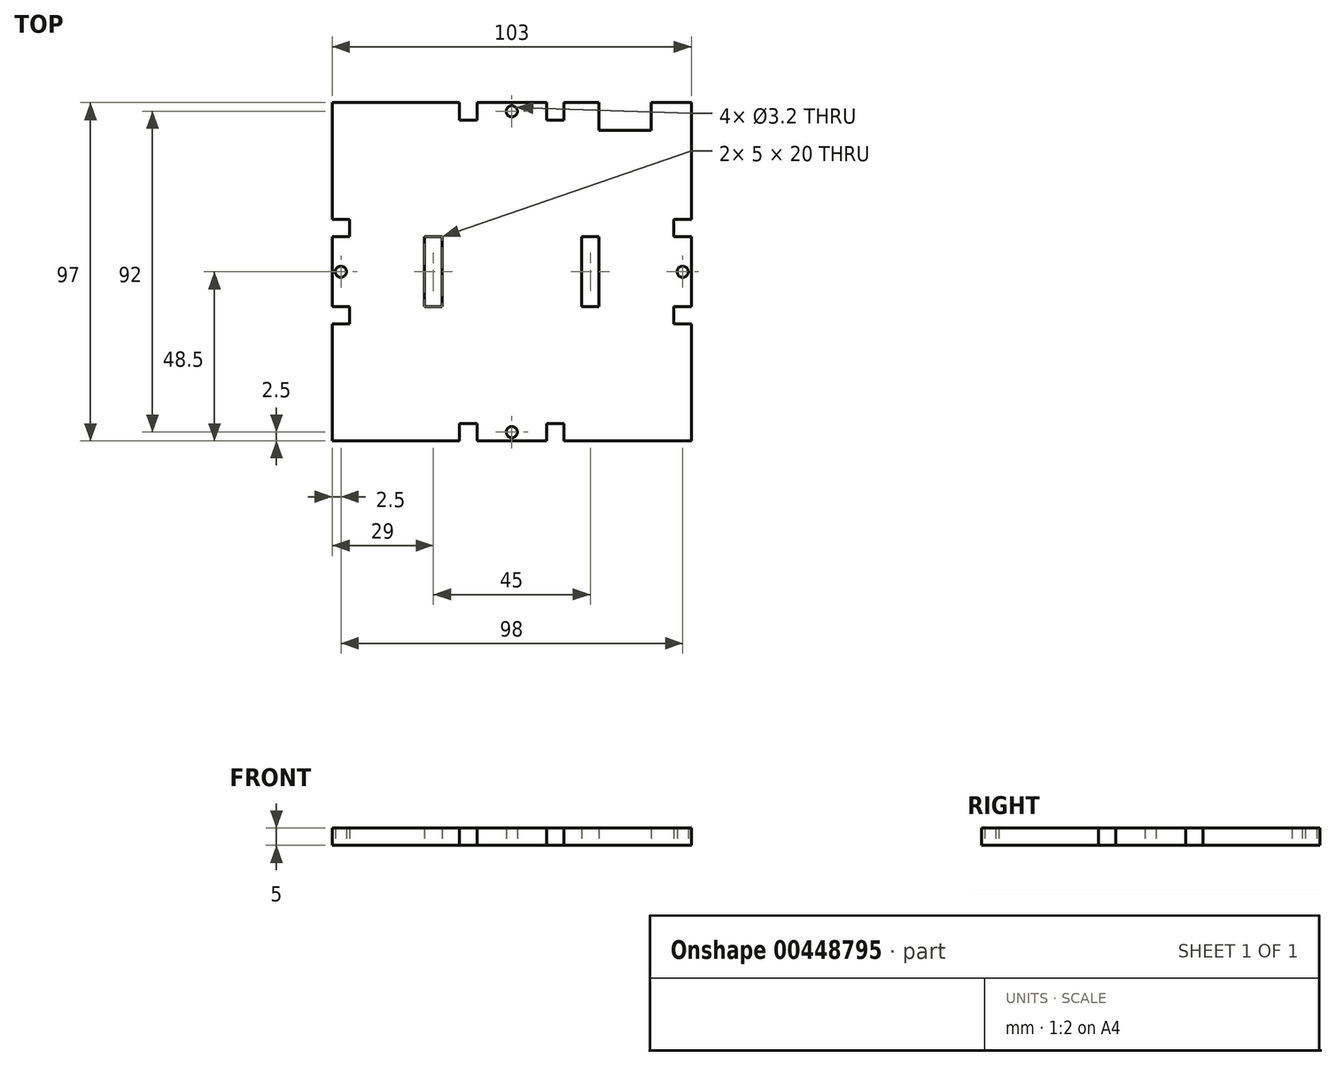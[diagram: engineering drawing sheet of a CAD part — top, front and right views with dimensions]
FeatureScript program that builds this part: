
annotation { "Feature Type Name" : "Feature", "Feature Type Description" : "" }
export const myFeature = defineFeature(function(context is Context, id is Id, definition is map)
    precondition{}
    {
        {
            assignVariable(context, id + "F0", {"name" : "thickness", "anyValue" : 5 * mm});
        }
        {
            var Q0;
            Q0=qCreatedBy(makeId("Top.planeOp"),FACE);
            var sketch = newSketch(context, id + "F1", { "sketchPlane" : qUnion([Q0])});
            skLineSegment(sketch, "E0.MirrorCS", {"start": v(41.5, 92) * mm, "end": v(41.5, 97) * mm});
            skPoint(sketch, "E1.MirrorP", {"position": v(41.5, 94.5) * mm});
            skLineSegment(sketch, "E2.MirrorCS", {"start": v(61.5, 92) * mm, "end": v(66.5, 92) * mm});
            skLineSegment(sketch, "E3.MirrorCS", {"start": v(36.5, 97) * mm, "end": v(36.5, 92) * mm});
            skLineSegment(sketch, "E4.MirrorCS", {"start": v(36.5, 92) * mm, "end": v(41.5, 92) * mm});
            skCircle(sketch, "E5.MirrorC", {"center": v(51.5, 94.5) * mm, "radius": 1.6 * mm});
            skLineSegment(sketch, "E6.MirrorCS", {"start": v(61.5, 97) * mm, "end": v(61.5, 92) * mm});
            skLineSegment(sketch, "E7.MirrorCS", {"start": v(66.5, 92) * mm, "end": v(66.5, 97) * mm});
            skLineSegment(sketch, "E8.MirrorCS", {"start": v(41.5, 97) * mm, "end": v(61.5, 97) * mm});
            skLineSegment(sketch, "E9.bottom", {"start": v(0, 0) * mm, "end": v(36.5, 0) * mm});
            skLineSegment(sketch, "E9.top", {"start": v(0, 97) * mm, "end": v(36.5, 97) * mm});
            skLineSegment(sketch, "E9.left", {"start": v(0, 0) * mm, "end": v(0, 33.5) * mm});
            skLineSegment(sketch, "E9.right", {"start": v(103, 0) * mm, "end": v(103, 33.5) * mm});
            skLineSegment(sketch, "E10", {"start": v(51.5, 0) * mm, "end": v(51.5, 97) * mm, "construction": true});
            skLineSegment(sketch, "E11", {"start": v(0, 48.5) * mm, "end": v(103, 48.5) * mm, "construction": true});
            skLineSegment(sketch, "E12.MirrorCS", {"start": v(41.5, 5) * mm, "end": v(41.5, 0) * mm});
            skLineSegment(sketch, "E13.MirrorCS", {"start": v(41.5, 0) * mm, "end": v(61.5, 0) * mm});
            skLineSegment(sketch, "E14.MirrorCS", {"start": v(61.5, 0) * mm, "end": v(61.5, 5) * mm});
            skLineSegment(sketch, "E15.MirrorCS", {"start": v(66.5, 5) * mm, "end": v(66.5, 0) * mm});
            skPoint(sketch, "E16.MirrorP", {"position": v(41.5, 2.5) * mm});
            skCircle(sketch, "E17.MirrorC", {"center": v(51.5, 2.5) * mm, "radius": 1.6 * mm});
            skLineSegment(sketch, "E18.MirrorCS", {"start": v(61.5, 5) * mm, "end": v(66.5, 5) * mm});
            skLineSegment(sketch, "E19.MirrorCS", {"start": v(36.5, 5) * mm, "end": v(41.5, 5) * mm});
            skLineSegment(sketch, "E20.MirrorCS", {"start": v(36.5, 0) * mm, "end": v(36.5, 5) * mm});
            skLineSegment(sketch, "E21.MirrorCS", {"start": v(5, 38.5) * mm, "end": v(0, 38.5) * mm});
            skPoint(sketch, "E22.MirrorP", {"position": v(2.5, 38.5) * mm});
            skLineSegment(sketch, "E23.MirrorCS", {"start": v(5, 58.5) * mm, "end": v(5, 63.5) * mm});
            skLineSegment(sketch, "E24.MirrorCS", {"start": v(0, 33.5) * mm, "end": v(5, 33.5) * mm});
            skLineSegment(sketch, "E25.MirrorCS", {"start": v(5, 33.5) * mm, "end": v(5, 38.5) * mm});
            skCircle(sketch, "E26.MirrorC", {"center": v(2.5, 48.5) * mm, "radius": 1.6 * mm});
            skLineSegment(sketch, "E27.MirrorCS", {"start": v(0, 58.5) * mm, "end": v(5, 58.5) * mm});
            skLineSegment(sketch, "E28.MirrorCS", {"start": v(5, 63.5) * mm, "end": v(0, 63.5) * mm});
            skLineSegment(sketch, "E29.MirrorCS", {"start": v(0, 38.5) * mm, "end": v(0, 58.5) * mm});
            skLineSegment(sketch, "E30.MirrorCS", {"start": v(98, 38.5) * mm, "end": v(103, 38.5) * mm});
            skPoint(sketch, "E31.MirrorP", {"position": v(100.5, 38.5) * mm});
            skCircle(sketch, "E32.MirrorC", {"center": v(100.5, 48.5) * mm, "radius": 1.6 * mm});
            skLineSegment(sketch, "E33.MirrorCS", {"start": v(98, 63.5) * mm, "end": v(103, 63.5) * mm});
            skLineSegment(sketch, "E34.MirrorCS", {"start": v(103, 33.5) * mm, "end": v(98, 33.5) * mm});
            skLineSegment(sketch, "E35.MirrorCS", {"start": v(98, 58.5) * mm, "end": v(98, 63.5) * mm});
            skLineSegment(sketch, "E36.MirrorCS", {"start": v(103, 38.5) * mm, "end": v(103, 58.5) * mm});
            skLineSegment(sketch, "E37.MirrorCS", {"start": v(98, 33.5) * mm, "end": v(98, 38.5) * mm});
            skLineSegment(sketch, "E38.MirrorCS", {"start": v(103, 58.5) * mm, "end": v(98, 58.5) * mm});
            skLineSegment(sketch, "E39.trimOffspring", {"start": v(66.5, 97) * mm, "end": v(76.5, 97) * mm});
            skLineSegment(sketch, "E40.trimOffspring", {"start": v(0, 63.5) * mm, "end": v(0, 97) * mm});
            skLineSegment(sketch, "E41.trimOffspring", {"start": v(103, 63.5) * mm, "end": v(103, 97) * mm});
            skLineSegment(sketch, "E42.trimOffspring", {"start": v(66.5, 0) * mm, "end": v(103, 0) * mm});
            skLineSegment(sketch, "E43", {"start": v(76.5, 97) * mm, "end": v(76.5, 89) * mm});
            skLineSegment(sketch, "E44", {"start": v(76.5, 89) * mm, "end": v(91.5, 89) * mm});
            skLineSegment(sketch, "E45", {"start": v(91.5, 89) * mm, "end": v(91.5, 97) * mm});
            skLineSegment(sketch, "E46.trimOffspring", {"start": v(91.5, 97) * mm, "end": v(103, 97) * mm});
            skLineSegment(sketch, "E47.bottom", {"start": v(26.5, 58.5) * mm, "end": v(31.5, 58.5) * mm});
            skLineSegment(sketch, "E47.top", {"start": v(26.5, 38.5) * mm, "end": v(31.5, 38.5) * mm});
            skLineSegment(sketch, "E47.left", {"start": v(26.5, 58.5) * mm, "end": v(26.5, 38.5) * mm});
            skLineSegment(sketch, "E47.right", {"start": v(31.5, 58.5) * mm, "end": v(31.5, 38.5) * mm});
            skPoint(sketch, "E48", {"position": v(31.5, 48.5) * mm});
            skPoint(sketch, "E49.MirrorP", {"position": v(71.5, 48.5) * mm});
            skLineSegment(sketch, "E50.MirrorCS", {"start": v(71.5, 58.5) * mm, "end": v(71.5, 38.5) * mm});
            skLineSegment(sketch, "E51.MirrorCS", {"start": v(76.5, 58.5) * mm, "end": v(76.5, 38.5) * mm});
            skLineSegment(sketch, "E52.MirrorCS", {"start": v(76.5, 58.5) * mm, "end": v(71.5, 58.5) * mm});
            skLineSegment(sketch, "E53.MirrorCS", {"start": v(76.5, 38.5) * mm, "end": v(71.5, 38.5) * mm});
            skSolve(sketch);
        }
        {
            var Q0;
            Q0=qSketchRegion(id+"F1",true);
            extrude(context, id + "F2", {"entities" : qUnion([Q0]), "depth" : getVariable(context, 'thickness')});
        }
    });
